# Revit family: DockEquipment_Leveler_Pentalift_MD-MU-MC
name_source: partatom
category: Specialty Equipment
units: mm (PartAtom-declared; Revit-internal decimal feet)

## family parameters
Cut with Voids When Loaded = No
Enable Cutting in Views = No
Host = Face
Maintain Annotation Orientation = No
Part Type = Normal
Room Calculation Point = No
Round Connector Dimension = Use Diameter
Shared = No

## types (1)
- DockEquipment_Leveler_Pentalift_MD-MU-MC
    Assembly Code = E1030300
    Capacity (Weight) = 100.00 kip
    Construction Details = http://www.arcat.com
    Default Elevation = 4' - 0"
    Description = Pentalift Dock Equipment as Specified
    Expected Lifespan (Years) = 0
    Keynote = 11160
    Maintenance Schedule (Months) = 0
    Manufacturer = Pentalift Equipment Corp.
    Manufacturer Fax = 519-763-2894
    Manufacturer Website = http://www.pentalift.com
    Material = Metal - Steel - Pentalift - Painted - Gray
    Max Angle = 10.00°
    Model = As Specified
    PF Length = 7' - 9 7/8"
    Product Data = http://www.arcat.com
    Revision = R1_1_2012
    Sales Information = http://www.pentalift.com
    Send Message = http://www.arcat.com Equipment Corp.&coid=34752&rep=119&fax=519-763-2894&mf=
    URL = http://www.pentalift.com
    Unit Depth = 1' - 7"
    Unit Length = 8' - 0"
    Unit Width = 6' - 0"
    Warranty Duration (Years) = 0

## geometry (parser evidence)
native form markers: Sweep x5
no freeform markers — native parametric forms only
